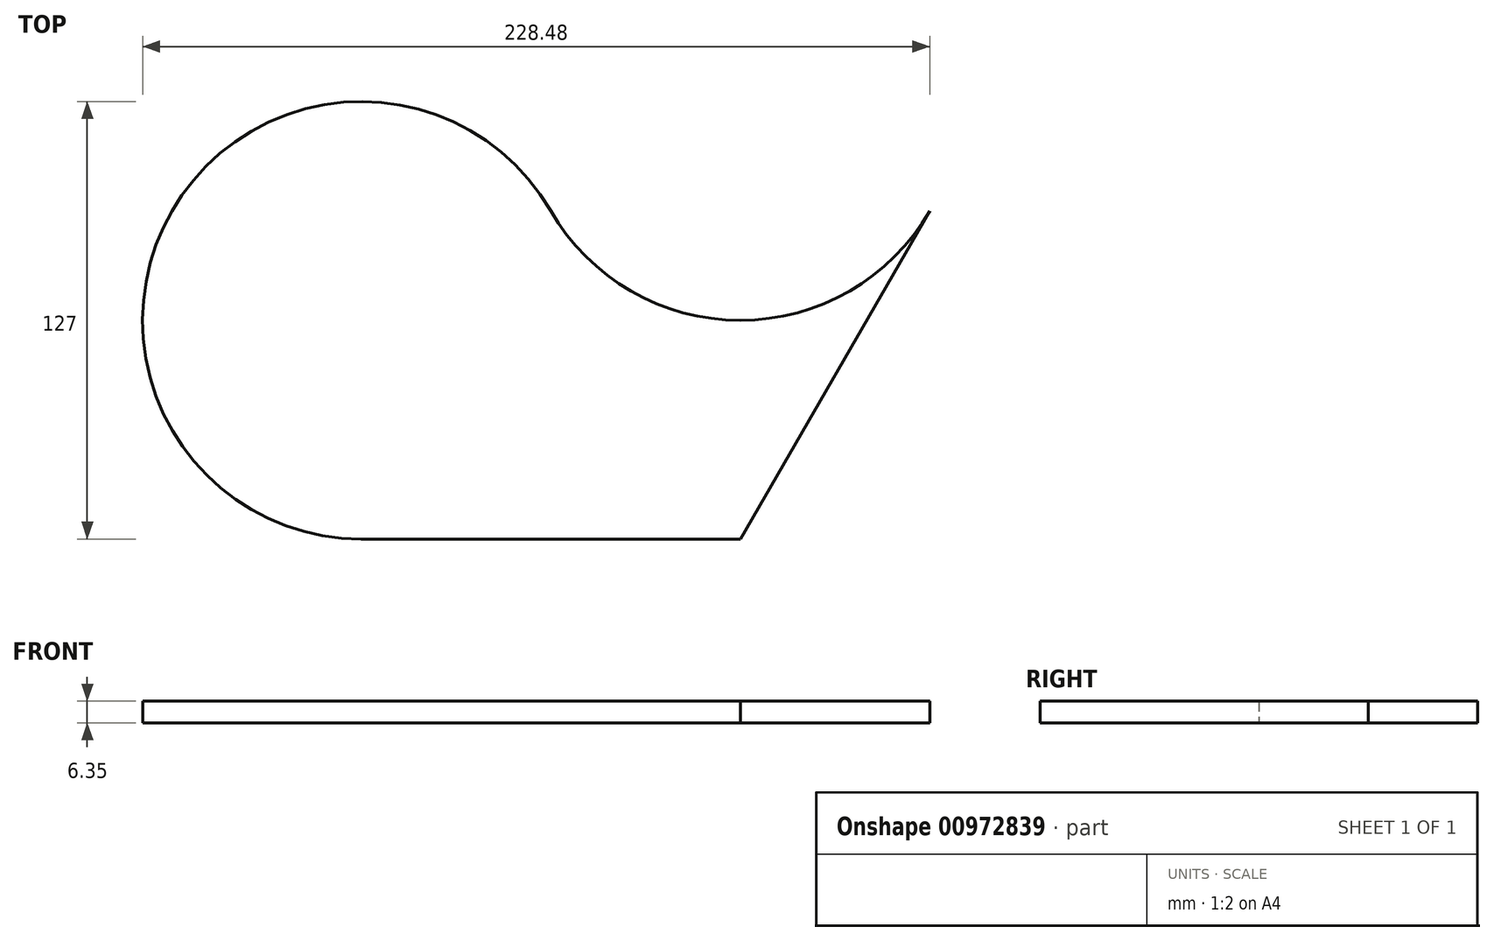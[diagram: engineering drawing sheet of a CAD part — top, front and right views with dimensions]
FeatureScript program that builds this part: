
annotation { "Feature Type Name" : "Feature", "Feature Type Description" : "" }
export const myFeature = defineFeature(function(context is Context, id is Id, definition is map)
    precondition{}
    {
        {
            var Q0;
            Q0=qCreatedBy(makeId("Top.planeOp"),FACE);
            var sketch = newSketch(context, id + "F0", { "sketchPlane" : qUnion([Q0])});
            skCircle(sketch, "E0", {"center": v(0, 0) * mm, "radius": 127 * mm, "construction": true});
            skLineSegment(sketch, "E1", {"start": v(0, 0) * mm, "end": v(0, 169.9) * mm, "construction": true});
            skCircle(sketch, "E2", {"center": v(0, 127) * mm, "radius": 63.5 * mm, "construction": true});
            skCircle(sketch, "E3.1.0", {"center": v(-109.99, 63.5) * mm, "radius": 63.5 * mm, "construction": true});
            skLineSegment(sketch, "E3.1.1", {"start": v(0, 0) * mm, "end": v(-147.13, 84.95) * mm, "construction": true});
            skCircle(sketch, "E3.2.0", {"center": v(-109.99, -63.5) * mm, "radius": 63.5 * mm, "construction": true});
            skLineSegment(sketch, "E3.2.1", {"start": v(0, 0) * mm, "end": v(-147.13, -84.95) * mm, "construction": true});
            skCircle(sketch, "E4.1.3.0", {"center": v(0, -127) * mm, "radius": 63.5 * mm, "construction": true});
            skLineSegment(sketch, "E4.2.3.0", {"start": v(0, 0) * mm, "end": v(0, -169.9) * mm, "construction": true});
            skCircle(sketch, "E4.1.4.0", {"center": v(109.99, -63.5) * mm, "radius": 63.5 * mm, "construction": true});
            skLineSegment(sketch, "E4.2.4.0", {"start": v(0, 0) * mm, "end": v(147.13, -84.95) * mm, "construction": true});
            skCircle(sketch, "E4.1.5.0", {"center": v(109.99, 63.5) * mm, "radius": 63.5 * mm, "construction": true});
            skLineSegment(sketch, "E4.2.5.0", {"start": v(0, 0) * mm, "end": v(147.13, 84.95) * mm, "construction": true});
            skSolve(sketch);
        }
        {
            var Q0;
            Q0=qCreatedBy(makeId("Top.planeOp"),FACE);
            var sketch = newSketch(context, id + "F1", { "sketchPlane" : qUnion([Q0])});
            skArc(sketch, "E5.0", {"start": v(-55, 95.25) * mm, "mid": v(-164.98, 95.25) * mm, "end": v(-109.99, 0) * mm});
            skArc(sketch, "E6.0", {"start": v(-55, 95.25) * mm, "mid": v(0, 63.5) * mm, "end": v(55, 95.25) * mm});
            skLineSegment(sketch, "E7", {"start": v(-109.99, 0) * mm, "end": v(0, 0) * mm});
            skLineSegment(sketch, "E8", {"start": v(0, 0) * mm, "end": v(55, 95.25) * mm});
            skSolve(sketch);
        }
        {
            var Q0;
            Q0=makeQuery(id+"F1.imprint","IMPRINT",FACE,{"disambiguationData":[TD([[makeQuery(id+"F1.imprint","IMPRINT",EDGE,{"derivedFrom":sQuery(id+"F1.wireOp",EDGE,"E5.0")}),1.0]])]});
            extrude(context, id + "F2", {"entities" : qUnion([Q0]), "depth" : 6.35 * mm, "offsetDistance" : 25.4 * mm});
        }
    });
